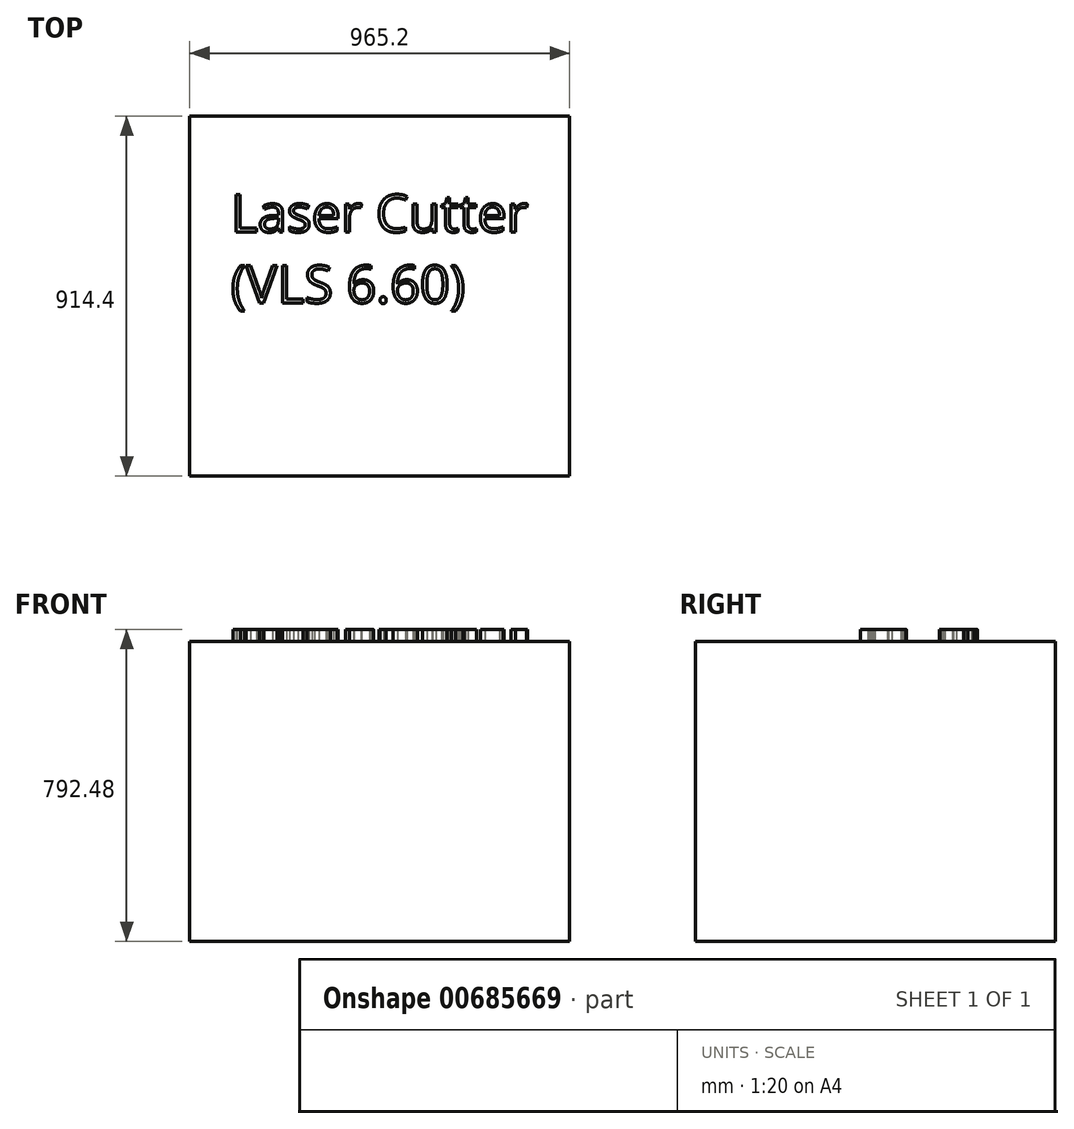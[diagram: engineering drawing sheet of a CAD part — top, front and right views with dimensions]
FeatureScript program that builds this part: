
annotation { "Feature Type Name" : "Feature", "Feature Type Description" : "" }
export const myFeature = defineFeature(function(context is Context, id is Id, definition is map)
    precondition{}
    {
        {
            var Q0;
            Q0=qCreatedBy(makeId("Top.planeOp"),FACE);
            var sketch = newSketch(context, id + "F0", { "sketchPlane" : qUnion([Q0])});
            skLineSegment(sketch, "E0.bottom", {"start": v(482.6, 457.2) * mm, "end": v(-482.6, 457.2) * mm});
            skLineSegment(sketch, "E0.top", {"start": v(482.6, -457.2) * mm, "end": v(-482.6, -457.2) * mm});
            skLineSegment(sketch, "E0.left", {"start": v(482.6, 457.2) * mm, "end": v(482.6, -457.2) * mm});
            skLineSegment(sketch, "E0.right", {"start": v(-482.6, 457.2) * mm, "end": v(-482.6, -457.2) * mm});
            skPoint(sketch, "E0.middle", {"position": v(0, 0) * mm});
            skSolve(sketch);
        }
        {
            var Q0;
            Q0 = qSketchRegion(id + "F0", true);
            extrude(context, id + "F1", {"entities" : qUnion([Q0]), "depth" : 762 * mm, "offsetDistance" : 30.48 * mm});
        }
        {
            var Q0;
            Q0=makeQuery(id+"F1.opExtrude","CAP_FACE",FACE,{"disambiguationData":[OSD([sQuery(id+"F0.wireOp",EDGE,"E0.bottom"),sQuery(id+"F0.wireOp",EDGE,"E0.top"),sQuery(id+"F0.wireOp",EDGE,"E0.left"),sQuery(id+"F0.wireOp",EDGE,"E0.right")])],"isStart":false});
            var sketch = newSketch(context, id + "F2", { "sketchPlane" : qUnion([Q0])});
            skText(sketch, "E1", { "text": "Laser Cutter\n(VLS 6.60)\n", "fontName": "OpenSans-Regular.ttf"});
            const initialGuessF2  = {"E1": [-0.3786, 0.16277, 1, 0, 0.09538]};
            skSetInitialGuess(sketch, initialGuessF2);
            skSolve(sketch);
        }
        {
            var Q0;
            Q0 = qSketchRegion(id + "F2", true);
            extrude(context, id + "F3", {"entities" : qUnion([Q0]), "operationType" : NewBodyOperationType.ADD, "depth" : 30.48 * mm, "offsetDistance" : 30.48 * mm});
        }
    });
